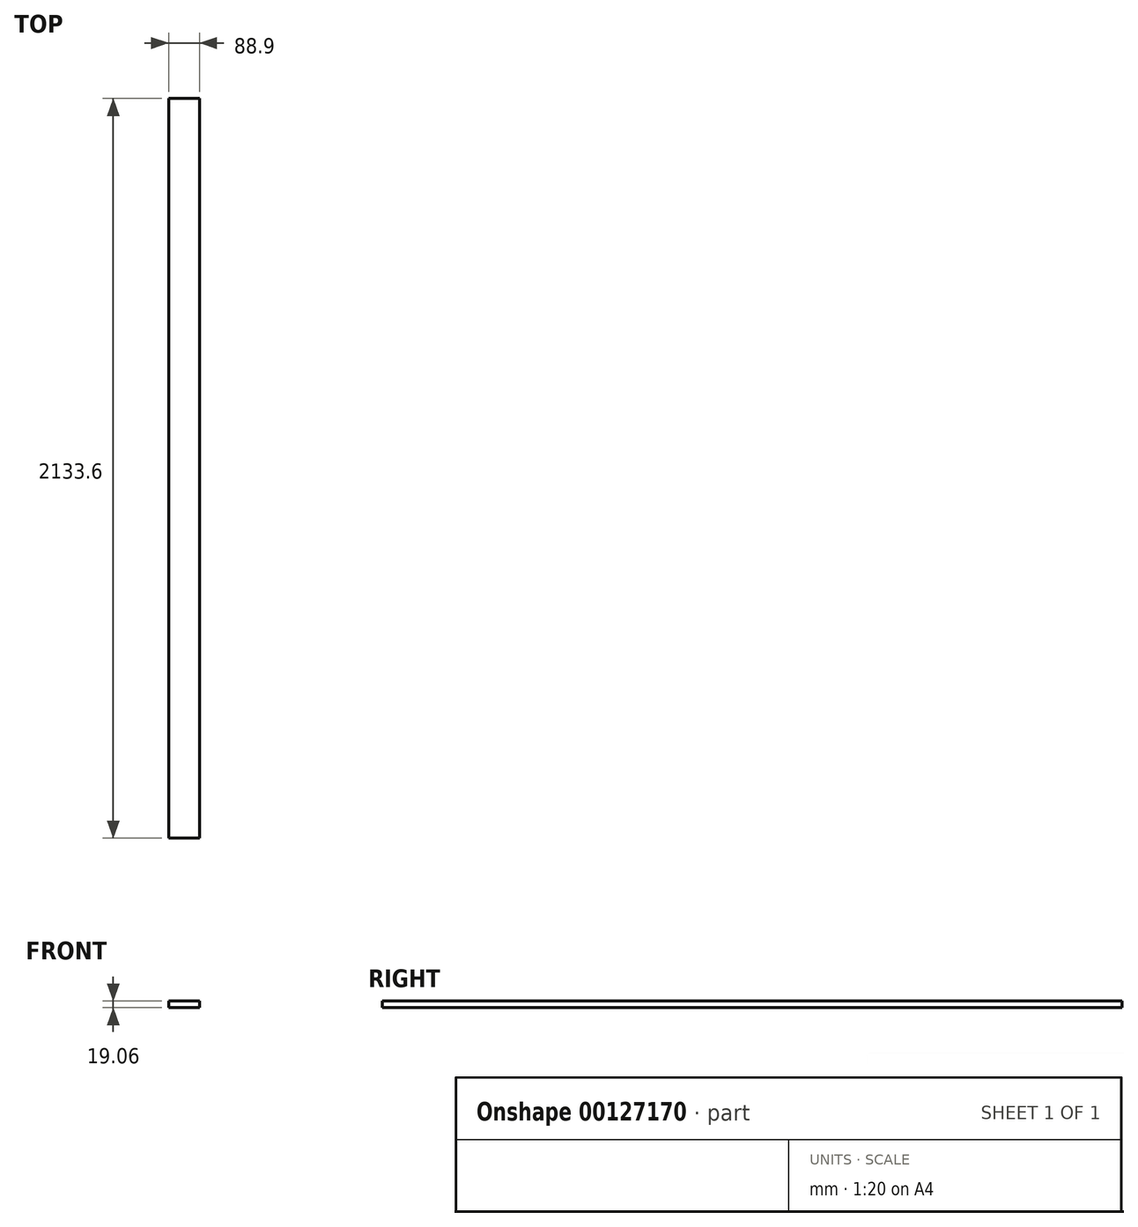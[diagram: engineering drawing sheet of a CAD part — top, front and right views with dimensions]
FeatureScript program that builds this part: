
annotation { "Feature Type Name" : "Feature", "Feature Type Description" : "" }
export const myFeature = defineFeature(function(context is Context, id is Id, definition is map)
    precondition{}
    {
        {
            var Q0;
            Q0=qCreatedBy(makeId("Front.planeOp"),FACE);
            var sketch = newSketch(context, id + "F0", { "sketchPlane" : qUnion([Q0])});
            skLineSegment(sketch, "E0.bottom", {"start": v(44.45, -9.52) * mm, "end": v(-44.45, -9.53) * mm});
            skLineSegment(sketch, "E0.top", {"start": v(44.45, 9.53) * mm, "end": v(-44.45, 9.53) * mm});
            skLineSegment(sketch, "E0.left", {"start": v(44.45, -9.52) * mm, "end": v(44.45, 9.53) * mm});
            skLineSegment(sketch, "E0.right", {"start": v(-44.45, -9.53) * mm, "end": v(-44.45, 9.53) * mm});
            skPoint(sketch, "E0.middle", {"position": v(0, 0) * mm});
            skSolve(sketch);
        }
        {
            var Q0;
            Q0=qSketchRegion(id+"F0",true);
            extrude(context, id + "F1", {"entities" : qUnion([Q0]), "depth" : 2133.6 * mm});
        }
    });
